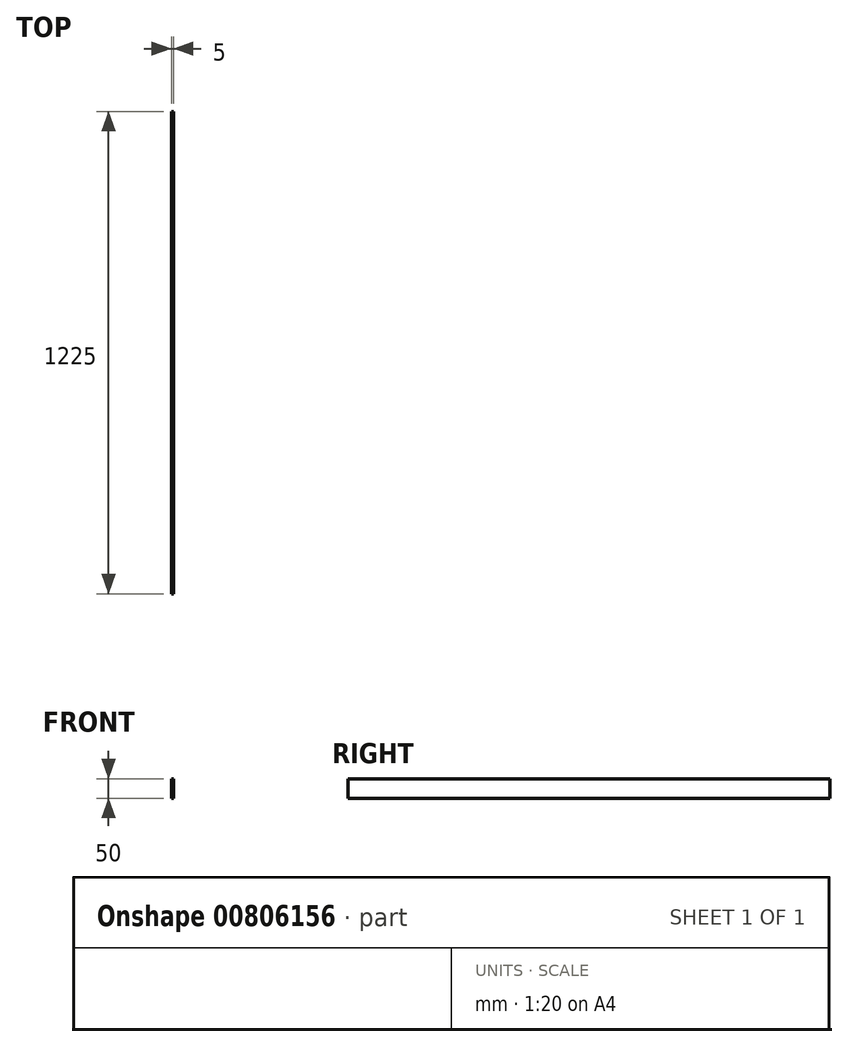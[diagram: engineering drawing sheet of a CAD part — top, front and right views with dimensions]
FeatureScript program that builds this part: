
annotation { "Feature Type Name" : "Feature", "Feature Type Description" : "" }
export const myFeature = defineFeature(function(context is Context, id is Id, definition is map)
    precondition{}
    {
        {
            var Q0;
            Q0=qCreatedBy(makeId("Front.planeOp"),FACE);
            var sketch = newSketch(context, id + "F0", { "sketchPlane" : qUnion([Q0])});
            skLineSegment(sketch, "E0.bottom", {"start": v(2.5, -25) * mm, "end": v(-2.5, -25) * mm});
            skLineSegment(sketch, "E0.top", {"start": v(2.5, 25) * mm, "end": v(-2.5, 25) * mm});
            skLineSegment(sketch, "E0.left", {"start": v(2.5, -25) * mm, "end": v(2.5, 25) * mm});
            skLineSegment(sketch, "E0.right", {"start": v(-2.5, -25) * mm, "end": v(-2.5, 25) * mm});
            skPoint(sketch, "E0.middle", {"position": v(0, 0) * mm});
            skSolve(sketch);
        }
        {
            var Q0;
            Q0=qSketchRegion(id+"F0",true);
            extrude(context, id + "F1", {"entities" : qUnion([Q0]), "depth" : 1225 * mm, "offsetDistance" : 25 * mm});
        }
    });
